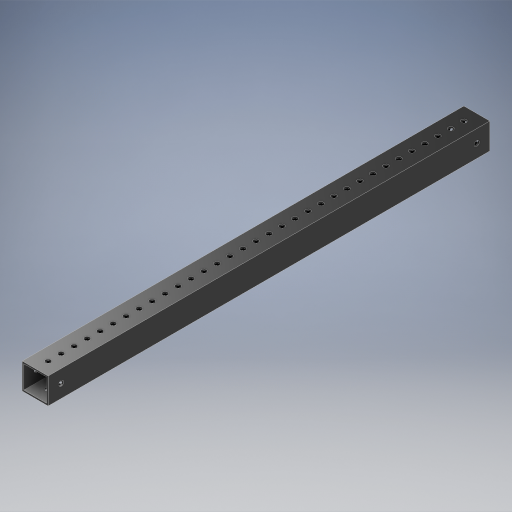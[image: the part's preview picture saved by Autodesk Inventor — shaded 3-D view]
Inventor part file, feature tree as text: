
AUTODESK INVENTOR PART (.ipt)
format: ipt  version: 2024.2 (Build 282272000, 272)  size: 811,008 bytes
history: native  units: in
note: dims shown in document units (in); Inventor stores cm internally (conversion verified against a paired STEP export)
features: other x13, extrude x9, hole x3, pattern_linear x3, mirror x3, sheet_metal_op x1, plane x1
ambient origin geometry x8: Origin, YZ Plane, XZ Plane, XY Plane, X Axis, Y Axis, Z Axis, Center Point
bodies: Solid1 (feature_tree)
feature tree (33):
  other  "Blocks"
  other  "Base Sketch"
  extrude  "Base"  Depth=1.0in
  extrude  "MAX Corner"  Depth=1.0in
  extrude  "MAX Corner Cut"  Depth=0.0625in
  extrude  "Scribe Lines"  Depth=0.0625in
  other  "Side Middle"
  other  "Top Middle"
  other  "Side Holes Sketch"
  hole  "Top Side Hole"  [1 undecoded]
  hole  "Mid Side Hole"  [1 undecoded]
  hole  "Btm Side Hole"  [1 undecoded]
  pattern_linear  "Side Holes"  Spacing1=0.04in  [1 undecoded]
  mirror  "Side Mirror"
  extrude  "MAXTube Hole"  Depth=0.04in
  extrude  "MAXTube Outside"  Depth=17.0in
  pattern_linear  "MAXTube Pattern"  Spacing1=0.0in  [1 undecoded]
  mirror  "MAXTube Mirror"
  extrude  "Left Top Hole"  Depth=17.0in
  extrude  "Mid Top Hole"  TaperAngle=0.0deg  [1 undecoded]
  extrude  "Right Top Hole"  TaperAngle=0.0deg  [1 undecoded]
  pattern_linear  "Top Holes"  Spacing1=0.005in  [1 undecoded]
  mirror  "Top Mirror"
  sheet_metal_op  "Corner"
  other  "MAXTube"
  plane  "Work Plane3"
  other  "Corner:5"
  other  "Corner:6"
  other  "Corner:7"
  other  "Corner:8"
  other  "MAXTube:1"
  other  "MAXTube:2"
  other  "MAXTube:3"
note: 8 required parameter values undecoded (feature->parameter linkage not recoverable at this tier; creation-order binding heuristic only, values carry confidence <= 0.55)
